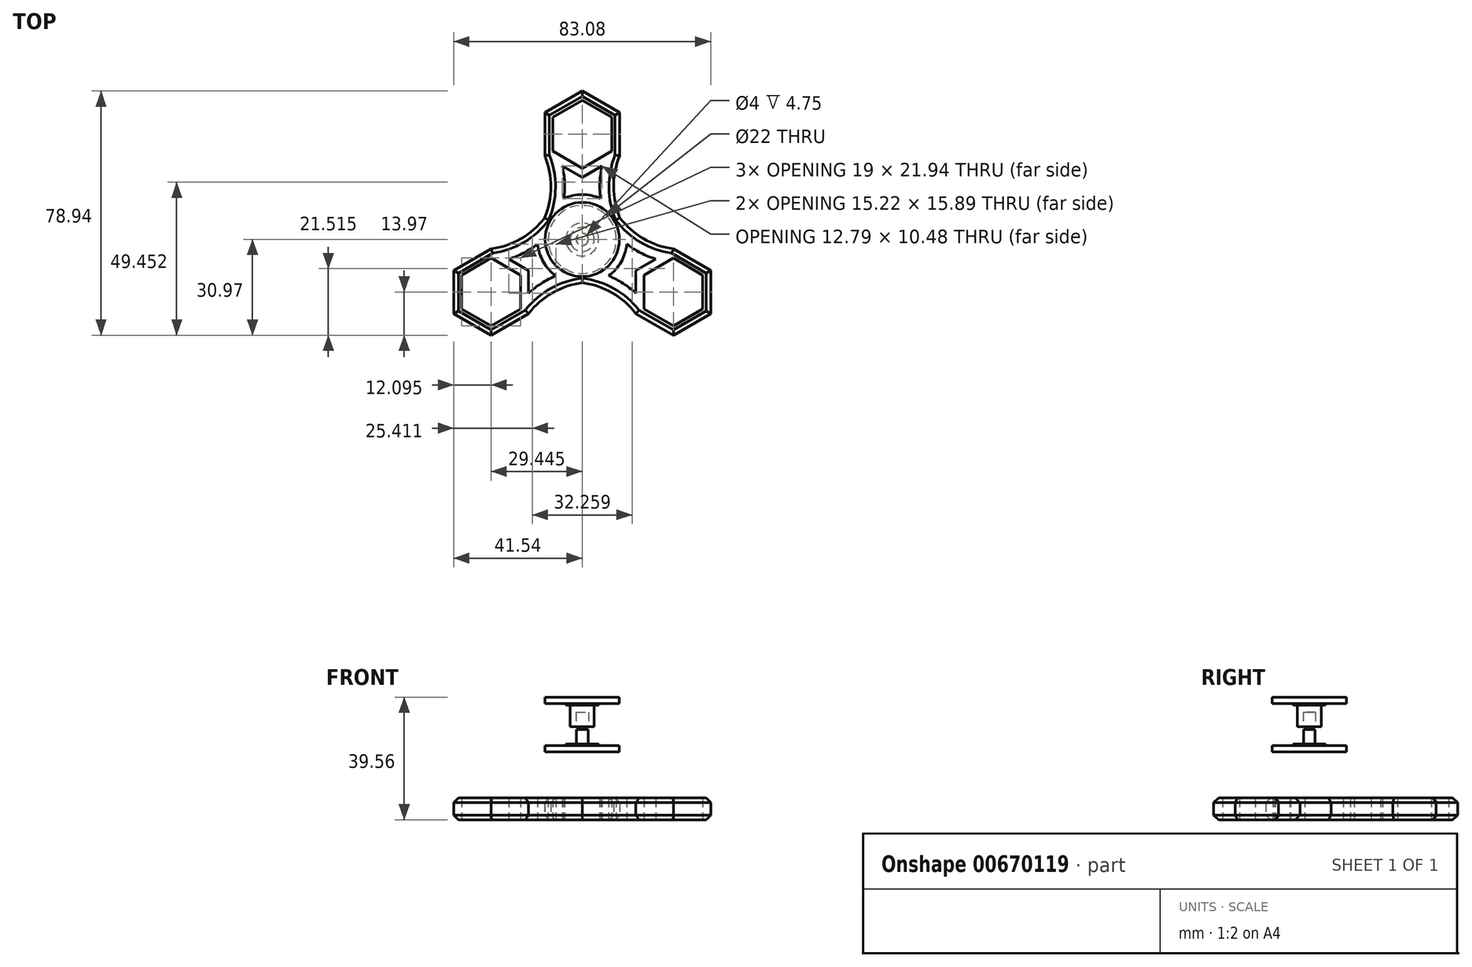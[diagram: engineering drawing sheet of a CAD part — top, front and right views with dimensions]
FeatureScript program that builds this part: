
annotation { "Feature Type Name" : "Feature", "Feature Type Description" : "" }
export const myFeature = defineFeature(function(context is Context, id is Id, definition is map)
    precondition{}
    {
        {
            var Q0;
            Q0=qCreatedBy(makeId("Top.planeOp"),FACE);
            var sketch = newSketch(context, id + "F0", { "sketchPlane" : qUnion([Q0])});
            skCircle(sketch, "E0", {"center": v(0, 0) * mm, "radius": 11 * mm});
            skArc(sketch, "E1", {"start": v(5.9, 13.24) * mm, "mid": v(0, 14.5) * mm, "end": v(-5.9, 13.24) * mm});
            skCircle(sketch, "E2", {"center": v(0, 0) * mm, "radius": 48.5 * mm, "construction": true});
            skCircle(sketch, "E3.cCircle", {"center": v(0, 34) * mm, "radius": 9.5 * mm, "construction": true});
            skLineSegment(sketch, "E3.0", {"start": v(9.5, 28.52) * mm, "end": v(0, 23.03) * mm});
            skLineSegment(sketch, "E3.1", {"start": v(0, 23.03) * mm, "end": v(-9.5, 28.52) * mm});
            skLineSegment(sketch, "E3.2", {"start": v(-9.5, 28.52) * mm, "end": v(-9.5, 39.48) * mm});
            skLineSegment(sketch, "E3.3", {"start": v(-9.5, 39.48) * mm, "end": v(0, 44.97) * mm});
            skLineSegment(sketch, "E3.4", {"start": v(0, 44.97) * mm, "end": v(9.5, 39.48) * mm});
            skLineSegment(sketch, "E3.5", {"start": v(9.5, 39.48) * mm, "end": v(9.5, 28.52) * mm});
            skPoint(sketch, "E3.0.midPoint", {"position": v(4.75, 25.77) * mm});
            skLineSegment(sketch, "E4.0", {"start": v(-12.1, 27.01) * mm, "end": v(-12.1, 40.99) * mm});
            skLineSegment(sketch, "E4.1", {"start": v(0, 47.97) * mm, "end": v(12.1, 40.99) * mm});
            skLineSegment(sketch, "E4.2", {"start": v(12.1, 40.99) * mm, "end": v(12.1, 27.01) * mm});
            skLineSegment(sketch, "E4.3", {"start": v(-12.1, 40.99) * mm, "end": v(0, 47.97) * mm});
            skLineSegment(sketch, "E4.4", {"start": v(6.4, 23.72) * mm, "end": v(0, 20.03) * mm});
            skLineSegment(sketch, "E4.5", {"start": v(0, 20.03) * mm, "end": v(-6.4, 23.72) * mm});
            skArc(sketch, "E5", {"start": v(12.1, 27.01) * mm, "mid": v(10.13, 17) * mm, "end": v(12.15, 7.01) * mm});
            skArc(sketch, "E6.MirrorCS", {"start": v(-12.1, 27.01) * mm, "mid": v(-10.13, 17) * mm, "end": v(-12.15, 7.01) * mm});
            skArc(sketch, "E7", {"start": v(5.9, 13.24) * mm, "mid": v(5.7, 18.5) * mm, "end": v(6.4, 23.72) * mm});
            skArc(sketch, "E8.MirrorCS", {"start": v(-5.9, 13.24) * mm, "mid": v(-5.7, 18.5) * mm, "end": v(-6.4, 23.72) * mm});
            skLineSegment(sketch, "E9.1.0", {"start": v(-41.54, -23.99) * mm, "end": v(-41.54, -10.01) * mm});
            skLineSegment(sketch, "E9.1.1", {"start": v(-38.94, -22.48) * mm, "end": v(-38.94, -11.52) * mm});
            skLineSegment(sketch, "E9.1.2", {"start": v(-29.44, -30.97) * mm, "end": v(-41.54, -23.99) * mm});
            skLineSegment(sketch, "E9.1.3", {"start": v(-29.44, -27.97) * mm, "end": v(-38.94, -22.48) * mm});
            skLineSegment(sketch, "E9.1.4", {"start": v(-19.94, -22.48) * mm, "end": v(-29.44, -27.97) * mm});
            skLineSegment(sketch, "E9.1.5", {"start": v(-17.34, -23.99) * mm, "end": v(-29.44, -30.97) * mm});
            skLineSegment(sketch, "E9.1.6", {"start": v(-17.34, -10.01) * mm, "end": v(-17.34, -17.4) * mm});
            skLineSegment(sketch, "E9.1.7", {"start": v(-19.94, -11.52) * mm, "end": v(-19.94, -22.48) * mm});
            skLineSegment(sketch, "E9.1.8", {"start": v(-29.44, -6.03) * mm, "end": v(-19.94, -11.52) * mm});
            skLineSegment(sketch, "E9.1.9", {"start": v(-38.94, -11.52) * mm, "end": v(-29.44, -6.03) * mm});
            skLineSegment(sketch, "E9.1.10", {"start": v(-41.54, -10.01) * mm, "end": v(-29.44, -3.03) * mm});
            skLineSegment(sketch, "E9.1.11", {"start": v(-23.74, -6.32) * mm, "end": v(-17.34, -10.01) * mm});
            skArc(sketch, "E9.1.12", {"start": v(-14.42, -1.51) * mm, "mid": v(-18.87, -4.32) * mm, "end": v(-23.74, -6.32) * mm});
            skArc(sketch, "E9.1.13", {"start": v(-29.44, -3.03) * mm, "mid": v(-19.8, 0.27) * mm, "end": v(-12.15, 7.01) * mm});
            skArc(sketch, "E9.1.14", {"start": v(-8.52, -11.73) * mm, "mid": v(-13.18, -14.18) * mm, "end": v(-17.34, -17.4) * mm});
            skArc(sketch, "E9.1.15", {"start": v(-17.34, -23.99) * mm, "mid": v(-9.67, -17.27) * mm, "end": v(0, -14.03) * mm});
            skLineSegment(sketch, "E9.2.0", {"start": v(41.54, -23.99) * mm, "end": v(29.44, -30.97) * mm});
            skLineSegment(sketch, "E9.2.1", {"start": v(38.94, -22.48) * mm, "end": v(29.44, -27.97) * mm});
            skLineSegment(sketch, "E9.2.2", {"start": v(41.54, -10.01) * mm, "end": v(41.54, -23.99) * mm});
            skLineSegment(sketch, "E9.2.3", {"start": v(38.94, -11.52) * mm, "end": v(38.94, -22.48) * mm});
            skLineSegment(sketch, "E9.2.4", {"start": v(29.44, -6.03) * mm, "end": v(38.94, -11.52) * mm});
            skLineSegment(sketch, "E9.2.5", {"start": v(29.44, -3.03) * mm, "end": v(41.54, -10.01) * mm});
            skLineSegment(sketch, "E9.2.6", {"start": v(17.34, -10.01) * mm, "end": v(23.74, -6.32) * mm});
            skLineSegment(sketch, "E9.2.7", {"start": v(19.94, -11.52) * mm, "end": v(29.44, -6.03) * mm});
            skLineSegment(sketch, "E9.2.8", {"start": v(19.94, -22.48) * mm, "end": v(19.94, -11.52) * mm});
            skLineSegment(sketch, "E9.2.9", {"start": v(29.44, -27.97) * mm, "end": v(19.94, -22.48) * mm});
            skLineSegment(sketch, "E9.2.10", {"start": v(29.44, -30.97) * mm, "end": v(17.34, -23.99) * mm});
            skLineSegment(sketch, "E9.2.11", {"start": v(17.34, -17.4) * mm, "end": v(17.34, -10.01) * mm});
            skArc(sketch, "E9.2.12", {"start": v(8.52, -11.73) * mm, "mid": v(13.18, -14.18) * mm, "end": v(17.34, -17.4) * mm});
            skArc(sketch, "E9.2.13", {"start": v(17.34, -23.99) * mm, "mid": v(9.67, -17.27) * mm, "end": v(0, -14.03) * mm});
            skArc(sketch, "E9.2.14", {"start": v(14.42, -1.51) * mm, "mid": v(18.87, -4.32) * mm, "end": v(23.74, -6.32) * mm});
            skArc(sketch, "E9.2.15", {"start": v(29.44, -3.03) * mm, "mid": v(19.8, 0.27) * mm, "end": v(12.15, 7.01) * mm});
            skArc(sketch, "E10.trimOffspring", {"start": v(8.52, -11.73) * mm, "mid": v(12.56, -7.25) * mm, "end": v(14.42, -1.51) * mm});
            skArc(sketch, "E11.trimOffspring", {"start": v(-14.42, -1.51) * mm, "mid": v(-12.56, -7.25) * mm, "end": v(-8.52, -11.73) * mm});
            skPoint(sketch, "E12", {"position": v(12.15, 7.01) * mm});
            skPoint(sketch, "E13.orphan", {"position": v(12.22, 6.92) * mm});
            skPoint(sketch, "E14.orphan", {"position": v(12.1, 7.13) * mm});
            skPoint(sketch, "E15.orphan", {"position": v(-0.12, -14.04) * mm});
            skPoint(sketch, "E16.orphan", {"position": v(0.12, -14.04) * mm});
            skPoint(sketch, "E17.orphan", {"position": v(-12.22, 6.92) * mm});
            skPoint(sketch, "E18.orphan", {"position": v(-12.1, 7.13) * mm});
            skSolve(sketch);
        }
        {
            var Q0;
            Q0=makeQuery(id+"F0.imprint","IMPRINT",FACE,{"disambiguationData":[TD([[makeQuery(id+"F0.imprint","IMPRINT",EDGE,{"derivedFrom":sQuery(id+"F0.wireOp",EDGE,"E0")}),-1.0]])]});
            extrude(context, id + "F1", {"entities" : qUnion([Q0]), "depth" : 7 * mm, "offsetDistance" : 25 * mm});
        }
        {
            var Q0;
            Q0=makeQuery(id+"F1.opExtrude","CAP_EDGE",EDGE,{"disambiguationData":[OSD([sQuery(id+"F0.wireOp",EDGE,"E6.MirrorCS")])],"isStart":false});
            var Q1;
            Q1=makeQuery(id+"F1.opExtrude","CAP_EDGE",EDGE,{"disambiguationData":[OSD([sQuery(id+"F0.wireOp",EDGE,"E4.0")])],"isStart":false});
            var Q2;
            Q2=makeQuery(id+"F1.opExtrude","CAP_EDGE",EDGE,{"disambiguationData":[OSD([sQuery(id+"F0.wireOp",EDGE,"E4.3")])],"isStart":false});
            var Q3;
            Q3=makeQuery(id+"F1.opExtrude","CAP_EDGE",EDGE,{"disambiguationData":[OSD([sQuery(id+"F0.wireOp",EDGE,"E9.1.13")])],"isStart":false});
            var Q4;
            Q4=makeQuery(id+"F1.opExtrude","CAP_EDGE",EDGE,{"disambiguationData":[OSD([sQuery(id+"F0.wireOp",EDGE,"E9.1.10")])],"isStart":false});
            var Q5;
            Q5=makeQuery(id+"F1.opExtrude","CAP_EDGE",EDGE,{"disambiguationData":[OSD([sQuery(id+"F0.wireOp",EDGE,"E9.1.0")])],"isStart":false});
            var Q6;
            Q6=makeQuery(id+"F1.opExtrude","CAP_EDGE",EDGE,{"disambiguationData":[OSD([sQuery(id+"F0.wireOp",EDGE,"E9.1.2")])],"isStart":false});
            var Q7;
            Q7=makeQuery(id+"F1.opExtrude","CAP_EDGE",EDGE,{"disambiguationData":[OSD([sQuery(id+"F0.wireOp",EDGE,"E9.1.2")])],"isStart":true});
            var Q8;
            Q8=makeQuery(id+"F1.opExtrude","CAP_EDGE",EDGE,{"disambiguationData":[OSD([sQuery(id+"F0.wireOp",EDGE,"E9.1.0")])],"isStart":true});
            var Q9;
            Q9=makeQuery(id+"F1.opExtrude","CAP_EDGE",EDGE,{"disambiguationData":[OSD([sQuery(id+"F0.wireOp",EDGE,"E9.1.5")])],"isStart":false});
            var Q10;
            Q10=makeQuery(id+"F1.opExtrude","CAP_EDGE",EDGE,{"disambiguationData":[OSD([sQuery(id+"F0.wireOp",EDGE,"E9.1.10")])],"isStart":true});
            var Q11;
            Q11=makeQuery(id+"F1.opExtrude","CAP_EDGE",EDGE,{"disambiguationData":[OSD([sQuery(id+"F0.wireOp",EDGE,"E9.1.15")])],"isStart":false});
            var Q12;
            Q12=makeQuery(id+"F1.opExtrude","CAP_EDGE",EDGE,{"disambiguationData":[OSD([sQuery(id+"F0.wireOp",EDGE,"E9.2.13")])],"isStart":false});
            var Q13;
            Q13=makeQuery(id+"F1.opExtrude","CAP_EDGE",EDGE,{"disambiguationData":[OSD([sQuery(id+"F0.wireOp",EDGE,"E9.2.13")])],"isStart":true});
            var Q14;
            Q14=makeQuery(id+"F1.opExtrude","CAP_EDGE",EDGE,{"disambiguationData":[OSD([sQuery(id+"F0.wireOp",EDGE,"E9.2.10")])],"isStart":true});
            var Q15;
            Q15=makeQuery(id+"F1.opExtrude","CAP_EDGE",EDGE,{"disambiguationData":[OSD([sQuery(id+"F0.wireOp",EDGE,"E9.2.10")])],"isStart":false});
            var Q16;
            Q16=makeQuery(id+"F1.opExtrude","CAP_EDGE",EDGE,{"disambiguationData":[OSD([sQuery(id+"F0.wireOp",EDGE,"E9.2.0")])],"isStart":false});
            var Q17;
            Q17=makeQuery(id+"F1.opExtrude","CAP_EDGE",EDGE,{"disambiguationData":[OSD([sQuery(id+"F0.wireOp",EDGE,"E9.2.2")])],"isStart":false});
            var Q18;
            Q18=makeQuery(id+"F1.opExtrude","CAP_EDGE",EDGE,{"disambiguationData":[OSD([sQuery(id+"F0.wireOp",EDGE,"E9.2.5")])],"isStart":false});
            var Q19;
            Q19=makeQuery(id+"F1.opExtrude","CAP_EDGE",EDGE,{"disambiguationData":[OSD([sQuery(id+"F0.wireOp",EDGE,"E9.2.15")])],"isStart":false});
            var Q20;
            Q20=makeQuery(id+"F1.opExtrude","CAP_EDGE",EDGE,{"disambiguationData":[OSD([sQuery(id+"F0.wireOp",EDGE,"E5")])],"isStart":false});
            var Q21;
            Q21=makeQuery(id+"F1.opExtrude","CAP_EDGE",EDGE,{"disambiguationData":[OSD([sQuery(id+"F0.wireOp",EDGE,"E6.MirrorCS")])],"isStart":true});
            var Q22;
            Q22=makeQuery(id+"F1.opExtrude","CAP_EDGE",EDGE,{"disambiguationData":[OSD([sQuery(id+"F0.wireOp",EDGE,"E9.1.13")])],"isStart":true});
            var Q23;
            Q23=makeQuery(id+"F1.opExtrude","CAP_EDGE",EDGE,{"disambiguationData":[OSD([sQuery(id+"F0.wireOp",EDGE,"E4.0")])],"isStart":true});
            var Q24;
            Q24=makeQuery(id+"F1.opExtrude","CAP_EDGE",EDGE,{"disambiguationData":[OSD([sQuery(id+"F0.wireOp",EDGE,"E4.3")])],"isStart":true});
            var Q25;
            Q25=makeQuery(id+"F1.opExtrude","CAP_EDGE",EDGE,{"disambiguationData":[OSD([sQuery(id+"F0.wireOp",EDGE,"E4.2")])],"isStart":false});
            var Q26;
            Q26=makeQuery(id+"F1.opExtrude","CAP_EDGE",EDGE,{"disambiguationData":[OSD([sQuery(id+"F0.wireOp",EDGE,"E4.1")])],"isStart":false});
            var Q27;
            Q27=makeQuery(id+"F1.opExtrude","CAP_EDGE",EDGE,{"disambiguationData":[OSD([sQuery(id+"F0.wireOp",EDGE,"E4.1")])],"isStart":true});
            var Q28;
            Q28=makeQuery(id+"F1.opExtrude","CAP_EDGE",EDGE,{"disambiguationData":[OSD([sQuery(id+"F0.wireOp",EDGE,"E4.2")])],"isStart":true});
            var Q29;
            Q29=makeQuery(id+"F1.opExtrude","CAP_EDGE",EDGE,{"disambiguationData":[OSD([sQuery(id+"F0.wireOp",EDGE,"E5")])],"isStart":true});
            var Q30;
            Q30=makeQuery(id+"F1.opExtrude","CAP_EDGE",EDGE,{"disambiguationData":[OSD([sQuery(id+"F0.wireOp",EDGE,"E9.1.5")])],"isStart":true});
            var Q31;
            Q31=makeQuery(id+"F1.opExtrude","CAP_EDGE",EDGE,{"disambiguationData":[OSD([sQuery(id+"F0.wireOp",EDGE,"E9.1.15")])],"isStart":true});
            var Q32;
            Q32=makeQuery(id+"F1.opExtrude","CAP_EDGE",EDGE,{"disambiguationData":[OSD([sQuery(id+"F0.wireOp",EDGE,"E9.2.15")])],"isStart":true});
            var Q33;
            Q33=makeQuery(id+"F1.opExtrude","CAP_EDGE",EDGE,{"disambiguationData":[OSD([sQuery(id+"F0.wireOp",EDGE,"E9.2.5")])],"isStart":true});
            var Q34;
            Q34=makeQuery(id+"F1.opExtrude","CAP_EDGE",EDGE,{"disambiguationData":[OSD([sQuery(id+"F0.wireOp",EDGE,"E9.2.2")])],"isStart":true});
            var Q35;
            Q35=makeQuery(id+"F1.opExtrude","CAP_EDGE",EDGE,{"disambiguationData":[OSD([sQuery(id+"F0.wireOp",EDGE,"E9.2.0")])],"isStart":true});
            chamfer(context, id + "F2", {"entities" : qUnion([Q0, Q1, Q2, Q3, Q4, Q5, Q6, Q7, Q8, Q9, Q10, Q11, Q12, Q13, Q14, Q15, Q16, Q17, Q18, Q19, Q20, Q21, Q22, Q23, Q24, Q25, Q26, Q27, Q28, Q29, Q30, Q31, Q32, Q33, Q34, Q35]), "width" : 1.5 * mm, "tangentPropagation" : true});
        }
        {
            var Q0;
            Q0=qCreatedBy(makeId("Front.planeOp"),FACE);
            var sketch = newSketch(context, id + "F3", { "sketchPlane" : qUnion([Q0])});
            skLineSegment(sketch, "E19", {"start": v(12, 39.56) * mm, "end": v(12, 37.56) * mm});
            skLineSegment(sketch, "E20", {"start": v(12, 37.56) * mm, "end": v(5.3, 37.56) * mm});
            skLineSegment(sketch, "E21", {"start": v(5.3, 37.56) * mm, "end": v(5.3, 37.06) * mm});
            skLineSegment(sketch, "E22", {"start": v(5.3, 37.06) * mm, "end": v(3.9, 37.06) * mm});
            skLineSegment(sketch, "E23", {"start": v(3.9, 37.06) * mm, "end": v(3.9, 30.06) * mm});
            skLineSegment(sketch, "E24", {"start": v(3.9, 30.06) * mm, "end": v(2, 30.06) * mm});
            skLineSegment(sketch, "E25", {"start": v(0, 34.81) * mm, "end": v(0, 38.35) * mm});
            skLineSegment(sketch, "E26", {"start": v(2, 30.06) * mm, "end": v(2, 34.81) * mm});
            skLineSegment(sketch, "E27", {"start": v(2, 34.81) * mm, "end": v(0, 34.81) * mm});
            skPoint(sketch, "E28.orphan", {"position": v(3.9, 30.06) * mm});
            skPoint(sketch, "E29.orphan", {"position": v(0, 39.56) * mm});
            skLineSegment(sketch, "E30", {"start": v(12, 39.56) * mm, "end": v(0, 39.56) * mm});
            skLineSegment(sketch, "E31", {"start": v(0, 39.56) * mm, "end": v(0, 38.35) * mm});
            skPoint(sketch, "E32.center.orphan", {"position": v(0, 98.35) * mm});
            skLineSegment(sketch, "E33", {"start": v(0, 29.1) * mm, "end": v(1.9, 29.1) * mm});
            skLineSegment(sketch, "E34", {"start": v(1.9, 29.1) * mm, "end": v(1.9, 24.46) * mm});
            skLineSegment(sketch, "E35", {"start": v(1.9, 24.46) * mm, "end": v(5.3, 24.46) * mm});
            skLineSegment(sketch, "E36", {"start": v(5.3, 24.46) * mm, "end": v(5.3, 23.96) * mm});
            skLineSegment(sketch, "E37", {"start": v(5.3, 23.96) * mm, "end": v(12, 23.96) * mm});
            skLineSegment(sketch, "E38", {"start": v(12, 23.96) * mm, "end": v(12, 21.96) * mm});
            skLineSegment(sketch, "E39", {"start": v(12, 21.96) * mm, "end": v(0, 21.96) * mm});
            skLineSegment(sketch, "E40", {"start": v(0, 21.96) * mm, "end": v(0, 29.1) * mm});
            skLineSegment(sketch, "E41", {"start": v(0, 69.31) * mm, "end": v(0, -64.18) * mm, "construction": true});
            skSolve(sketch);
        }
        {
            var Q0;
            Q0=makeQuery(id+"F3.imprint","IMPRINT",FACE,{"disambiguationData":[TD([[makeQuery(id+"F3.imprint","IMPRINT",EDGE,{"derivedFrom":sQuery(id+"F3.wireOp",EDGE,"E19")}),-1.0]])]});
            var Q1;
            Q1=sQuery(id+"F3.wireOp",EDGE,"E25");
            revolve(context, id + "F4", {"entities" : qUnion([Q0]), "axis" : qUnion([Q1]), "revolveType" : RevolveType.FULL});
        }
        {
            var Q0;
            Q0 = qSketchRegion(id + "F3", true);
            var Q1;
            Q1=makeQuery(id+"F4.opRevolve","SWEPT_FACE",FACE,{"disambiguationData":[OSD([sQuery(id+"F3.wireOp",EDGE,"E23")])]});
            revolve(context, id + "F5", {"operationType" : NewBodyOperationType.ADD, "surfaceOperationType" : NewSurfaceOperationType.NEW, "entities" : qUnion([Q0]), "axis" : qUnion([Q1]), "revolveType" : RevolveType.FULL});
        }
    });
